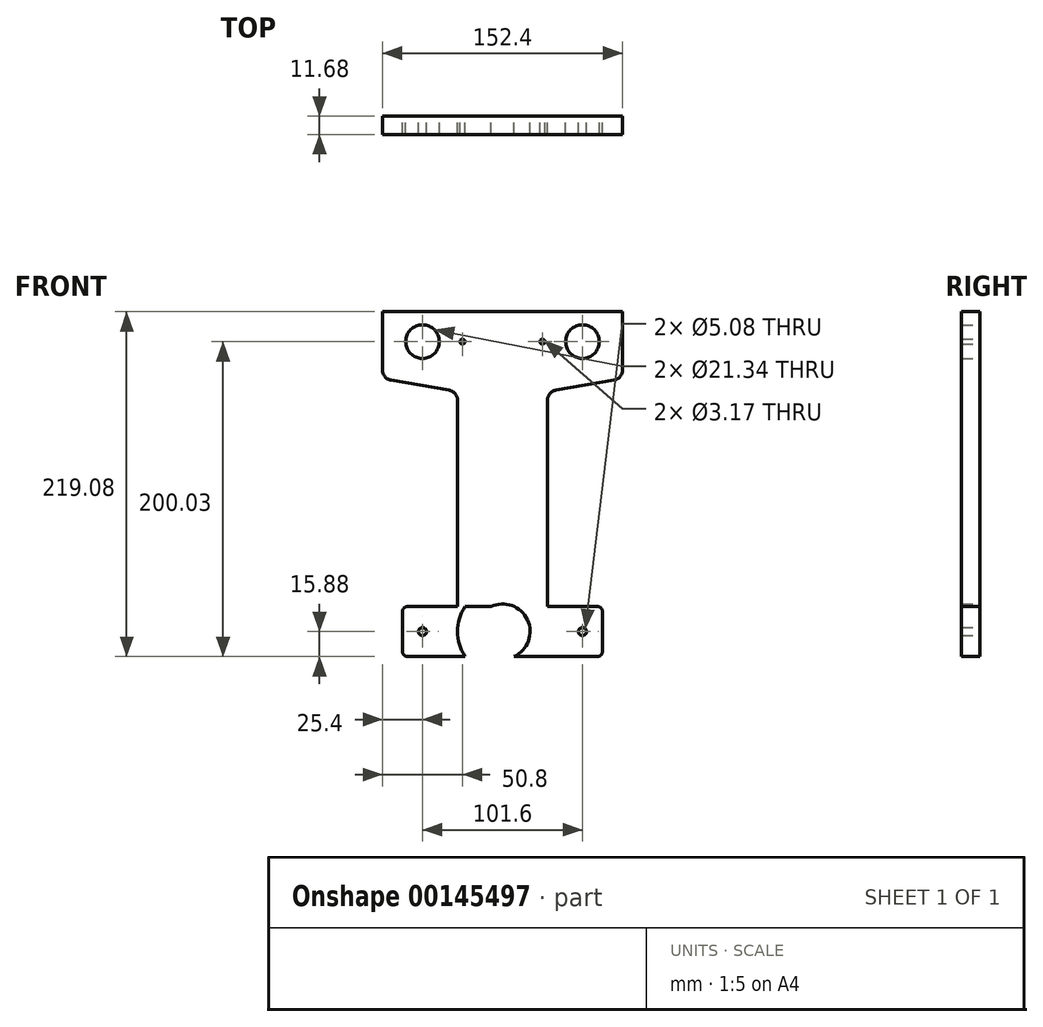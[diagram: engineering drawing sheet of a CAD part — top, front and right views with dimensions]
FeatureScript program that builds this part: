
annotation { "Feature Type Name" : "Feature", "Feature Type Description" : "" }
export const myFeature = defineFeature(function(context is Context, id is Id, definition is map)
    precondition{}
    {
        {
            var Q0;
            Q0=qCreatedBy(makeId("Front.planeOp"),FACE);
            var sketch = newSketch(context, id + "F0", { "sketchPlane" : qUnion([Q0])});
            skCircle(sketch, "E0", {"center": v(0, 0) * mm, "radius": 17.53 * mm});
            skCircle(sketch, "E1", {"center": v(0, 0) * mm, "radius": 28.58 * mm});
            skLineSegment(sketch, "E2.bottom", {"start": v(-60.33, 15.88) * mm, "end": v(60.33, 15.87) * mm});
            skLineSegment(sketch, "E2.top", {"start": v(-60.32, -15.87) * mm, "end": v(60.32, -15.87) * mm});
            skLineSegment(sketch, "E2.left", {"start": v(-63.5, 12.7) * mm, "end": v(-63.5, -12.7) * mm});
            skLineSegment(sketch, "E2.right", {"start": v(63.5, 12.7) * mm, "end": v(63.5, -12.7) * mm});
            skPoint(sketch, "E3", {"position": v(-63.5, 0) * mm});
            skPoint(sketch, "E4", {"position": v(63.5, 0) * mm});
            skPoint(sketch, "E5", {"position": v(0, 15.87) * mm});
            skPoint(sketch, "E6", {"position": v(0, -15.87) * mm});
            skCircle(sketch, "E7", {"center": v(-50.8, 0) * mm, "radius": 2.54 * mm});
            skCircle(sketch, "E8", {"center": v(50.8, 0) * mm, "radius": 2.54 * mm});
            skLineSegment(sketch, "E9", {"start": v(-17.53, 0) * mm, "end": v(-17.53, 203.2) * mm, "construction": true});
            skLineSegment(sketch, "E10", {"start": v(17.53, 0) * mm, "end": v(17.53, 203.2) * mm, "construction": true});
            skLineSegment(sketch, "E11", {"start": v(-17.53, 203.2) * mm, "end": v(17.53, 203.2) * mm});
            skLineSegment(sketch, "E12", {"start": v(-17.53, 203.2) * mm, "end": v(-76.2, 203.2) * mm});
            skLineSegment(sketch, "E13", {"start": v(17.53, 203.2) * mm, "end": v(76.2, 203.2) * mm});
            skLineSegment(sketch, "E14", {"start": v(-28.58, 0) * mm, "end": v(-28.57, 147.06) * mm});
            skLineSegment(sketch, "E15", {"start": v(28.58, 0) * mm, "end": v(28.58, 147.06) * mm});
            skLineSegment(sketch, "E16", {"start": v(-76.2, 203.2) * mm, "end": v(-76.2, 166) * mm});
            skLineSegment(sketch, "E17", {"start": v(76.2, 203.2) * mm, "end": v(76.2, 166) * mm});
            skLineSegment(sketch, "E18", {"start": v(-70.93, 159.74) * mm, "end": v(-33.84, 153.31) * mm});
            skLineSegment(sketch, "E19", {"start": v(33.84, 153.31) * mm, "end": v(70.93, 159.74) * mm});
            skPoint(sketch, "E20.visualSharp", {"position": v(-76.2, 160.66) * mm});
            skArc(sketch, "E20.filletArc", {"start": v(-76.2, 166) * mm, "mid": v(-74.7, 161.91) * mm, "end": v(-70.93, 159.74) * mm});
            skPoint(sketch, "E21.visualSharp", {"position": v(-28.57, 152.4) * mm});
            skArc(sketch, "E21.filletArc", {"start": v(-28.57, 147.06) * mm, "mid": v(-30.07, 151.14) * mm, "end": v(-33.84, 153.31) * mm});
            skPoint(sketch, "E22.visualSharp", {"position": v(28.58, 152.4) * mm});
            skArc(sketch, "E22.filletArc", {"start": v(33.84, 153.31) * mm, "mid": v(30.07, 151.14) * mm, "end": v(28.57, 147.06) * mm});
            skPoint(sketch, "E23.visualSharp", {"position": v(76.2, 160.66) * mm});
            skArc(sketch, "E23.filletArc", {"start": v(70.93, 159.74) * mm, "mid": v(74.7, 161.91) * mm, "end": v(76.2, 166) * mm});
            skPoint(sketch, "E24.visualSharp", {"position": v(-63.5, 15.88) * mm});
            skArc(sketch, "E24.filletArc", {"start": v(-60.33, 15.87) * mm, "mid": v(-62.57, 14.95) * mm, "end": v(-63.5, 12.7) * mm});
            skPoint(sketch, "E25.visualSharp", {"position": v(-63.5, -15.87) * mm});
            skArc(sketch, "E25.filletArc", {"start": v(-63.5, -12.7) * mm, "mid": v(-62.57, -14.95) * mm, "end": v(-60.32, -15.88) * mm});
            skPoint(sketch, "E26.visualSharp", {"position": v(63.5, 15.88) * mm});
            skArc(sketch, "E26.filletArc", {"start": v(63.5, 12.7) * mm, "mid": v(62.57, 14.95) * mm, "end": v(60.33, 15.87) * mm});
            skPoint(sketch, "E27.visualSharp", {"position": v(63.5, -15.88) * mm});
            skArc(sketch, "E27.filletArc", {"start": v(60.32, -15.88) * mm, "mid": v(62.57, -14.95) * mm, "end": v(63.5, -12.7) * mm});
            skCircle(sketch, "E28", {"center": v(-50.8, 184.15) * mm, "radius": 10.67 * mm});
            skCircle(sketch, "E29", {"center": v(-25.4, 184.15) * mm, "radius": 1.59 * mm});
            skCircle(sketch, "E30", {"center": v(25.4, 184.15) * mm, "radius": 1.59 * mm});
            skCircle(sketch, "E31", {"center": v(50.8, 184.15) * mm, "radius": 10.67 * mm});
            skPoint(sketch, "E32", {"position": v(-76.2, 184.15) * mm});
            skSolve(sketch);
        }
        {
            var Q0;
            Q0=makeQuery(id+"F0.imprint","IMPRINT",FACE,{"disambiguationData":[TD([[makeQuery(id+"F0.imprint","IMPRINT",EDGE,{"derivedFrom":sQuery(id+"F0.wireOp",EDGE,"E11")}),-1.0]])]});
            var Q1;
            Q1=makeQuery(id+"F0.imprint","IMPRINT",FACE,{"disambiguationData":[TD([[makeQuery(id+"F0.imprint","IMPRINT",EDGE,{"derivedFrom":sQuery(id+"F0.wireOp",EDGE,"E2.left")}),1.0]])]});
            var Q2;
            Q2=makeQuery(id+"F0.imprint","IMPRINT",FACE,{"disambiguationData":[TD([[makeQuery(id+"F0.imprint","IMPRINT",EDGE,{"derivedFrom":sQuery(id+"F0.wireOp",EDGE,"E2.right")}),-1.0]])]});
            var Q3;
            {var subQ0=sQuery(id+"F0.wireOp",EDGE,"E2.top");var subQ1=sQuery(id+"F0.wireOp",EDGE,"E0");var subQ2=makeQuery(id+"F0.imprint","INTERSECT",VERTEX,{"disambiguationData":[OD(0.0)],"derivedFrom":[subQ1,subQ0]});Q3=makeQuery(id+"F0.imprint","IMPRINT",FACE,{"disambiguationData":[TD([[makeQuery(id+"F0.imprint","IMPRINT",EDGE,{"disambiguationData":[TD([[subQ2,-1.0]])],"derivedFrom":subQ1}),-1.0]])]});}
            var Q4;
            {var subQ0=sQuery(id+"F0.wireOp",EDGE,"E2.bottom");var subQ1=sQuery(id+"F0.wireOp",EDGE,"E0");var subQ2=makeQuery(id+"F0.imprint","INTERSECT",VERTEX,{"disambiguationData":[OD(0.0)],"derivedFrom":[subQ1,subQ0]});Q4=makeQuery(id+"F0.imprint","IMPRINT",FACE,{"disambiguationData":[TD([[makeQuery(id+"F0.imprint","IMPRINT",EDGE,{"disambiguationData":[TD([[subQ2,-1.0]])],"derivedFrom":subQ1}),-1.0]])]});}
            var Q5;
            {var subQ0=sQuery(id+"F0.wireOp",EDGE,"E2.bottom");var subQ1=sQuery(id+"F0.wireOp",EDGE,"E0");var subQ2=makeQuery(id+"F0.imprint","INTERSECT",VERTEX,{"disambiguationData":[OD(0.0)],"derivedFrom":[subQ1,subQ0]});Q5=makeQuery(id+"F0.imprint","IMPRINT",FACE,{"disambiguationData":[TD([[makeQuery(id+"F0.imprint","IMPRINT",EDGE,{"disambiguationData":[TD([[subQ2,1.0]])],"derivedFrom":subQ1}),-1.0]])]});}
            var Q6;
            {var subQ0=sQuery(id+"F0.wireOp",EDGE,"E2.bottom");var subQ1=sQuery(id+"F0.wireOp",EDGE,"E0");var subQ2=makeQuery(id+"F0.imprint","INTERSECT",VERTEX,{"disambiguationData":[OD(1.0)],"derivedFrom":[subQ1,subQ0]});Q6=makeQuery(id+"F0.imprint","IMPRINT",FACE,{"disambiguationData":[TD([[makeQuery(id+"F0.imprint","IMPRINT",EDGE,{"disambiguationData":[TD([[subQ2,1.0]])],"derivedFrom":subQ1}),-1.0]])]});}
            var Q7;
            {var subQ0=sQuery(id+"F0.wireOp",EDGE,"E14");var subQ1=sQuery(id+"F0.wireOp",EDGE,"E1");var subQ2=makeQuery(id+"F0.imprint","INTERSECT",VERTEX,{"derivedFrom":[subQ1,subQ0]});Q7=makeQuery(id+"F0.imprint","IMPRINT",FACE,{"disambiguationData":[TD([[makeQuery(id+"F0.imprint","IMPRINT",EDGE,{"disambiguationData":[TD([[subQ2,1.0]])],"derivedFrom":subQ1}),-1.0]])]});}
            var Q8;
            {var subQ0=sQuery(id+"F0.wireOp",EDGE,"E15");var subQ1=sQuery(id+"F0.wireOp",EDGE,"E1");var subQ2=makeQuery(id+"F0.imprint","INTERSECT",VERTEX,{"derivedFrom":[subQ1,subQ0]});Q8=makeQuery(id+"F0.imprint","IMPRINT",FACE,{"disambiguationData":[TD([[makeQuery(id+"F0.imprint","IMPRINT",EDGE,{"disambiguationData":[TD([[subQ2,-1.0]])],"derivedFrom":subQ1}),-1.0]])]});}
            extrude(context, id + "F1", {"entities" : qUnion([Q0, Q1, Q2, Q3, Q4, Q5, Q6, Q7, Q8]), "depth" : 11.68 * mm});
        }
    });
